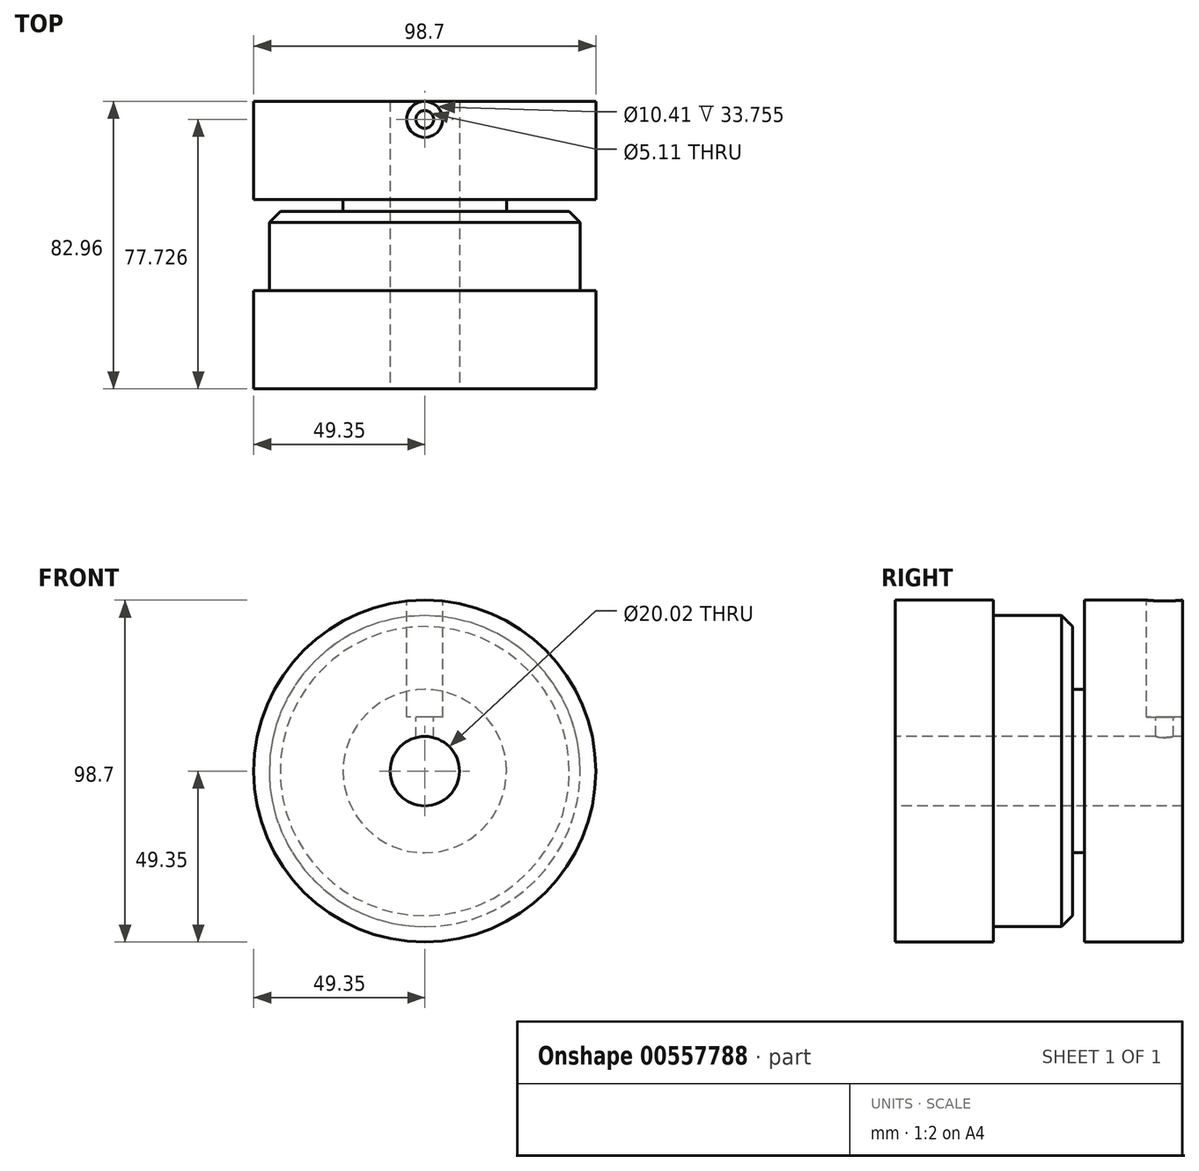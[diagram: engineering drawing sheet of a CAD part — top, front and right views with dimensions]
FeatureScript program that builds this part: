
annotation { "Feature Type Name" : "Feature", "Feature Type Description" : "" }
export const myFeature = defineFeature(function(context is Context, id is Id, definition is map)
    precondition{}
    {
        {
            var Q0;
            Q0=qCreatedBy(makeId("Right.planeOp"),FACE);
            var sketch = newSketch(context, id + "F0", { "sketchPlane" : qUnion([Q0])});
            skLineSegment(sketch, "E0", {"start": v(-35.21, 0) * mm, "end": v(33.24, 0) * mm, "construction": true});
            skLineSegment(sketch, "E1", {"start": v(0, 10) * mm, "end": v(-41.48, 10) * mm});
            skLineSegment(sketch, "E2", {"start": v(-41.48, 10) * mm, "end": v(-41.48, 49.35) * mm});
            skLineSegment(sketch, "E3", {"start": v(-41.48, 49.35) * mm, "end": v(-13.14, 49.35) * mm});
            skLineSegment(sketch, "E4", {"start": v(-13.14, 49.35) * mm, "end": v(-13.14, 44.88) * mm});
            skLineSegment(sketch, "E5", {"start": v(-13.14, 44.88) * mm, "end": v(9.72, 44.88) * mm});
            skLineSegment(sketch, "E6", {"start": v(0, 44.88) * mm, "end": v(0, 10) * mm, "construction": true});
            skLineSegment(sketch, "E7.MirrorCS", {"start": v(13.14, 49.35) * mm, "end": v(13.14, 23.57) * mm});
            skLineSegment(sketch, "E8.MirrorCS", {"start": v(41.48, 49.35) * mm, "end": v(13.14, 49.35) * mm});
            skLineSegment(sketch, "E9.MirrorCS", {"start": v(41.48, 10) * mm, "end": v(41.48, 49.35) * mm});
            skLineSegment(sketch, "E10.MirrorCS", {"start": v(0, 10) * mm, "end": v(41.48, 10) * mm});
            skLineSegment(sketch, "E11", {"start": v(9.72, 44.88) * mm, "end": v(9.72, 23.57) * mm});
            skLineSegment(sketch, "E12", {"start": v(9.72, 23.57) * mm, "end": v(14.35, 23.57) * mm});
            skPoint(sketch, "E13.orphan", {"position": v(0, 44.88) * mm});
            skSolve(sketch);
        }
        {
            var Q0;
            Q0=qSketchRegion(id+"F0",true);
            var Q1;
            Q1=sQuery(id+"F0.wireOp",EDGE,"E0");
            revolve(context, id + "F1", {"entities" : qUnion([Q0]), "axis" : qUnion([Q1]), "revolveType" : RevolveType.FULL});
        }
        {
            var Q0;
            Q0=makeQuery(id+"F1.opRevolve","SWEPT_EDGE",EDGE,{"disambiguationData":[OSD([sQuery(id+"F0.wireOp",EDGE,"cf1fef12-5ac8-4b01-91cc-4780af7254460.MirrorCS"),sQuery(id+"F0.wireOp",EDGE,"5POYRYxj-56Jz-sZJ7-dkSz-zXBiMIf3wF9C")])]});
            var Q1;
            Q1=makeQuery(id+"F1.opRevolve","SWEPT_EDGE",EDGE,{"disambiguationData":[OSD([sQuery(id+"F0.wireOp",EDGE,"E5"),sQuery(id+"F0.wireOp",EDGE,"E11")])]});
            chamfer(context, id + "F2", {"entities" : qUnion([Q0, Q1]), "width" : 3.17 * mm, "tangentPropagation" : true});
        }
        {
            var Q0;
            Q0=makeQuery(id+"F1.opRevolve","SWEPT_EDGE",EDGE,{"disambiguationData":[OSD([sQuery(id+"F0.wireOp",EDGE,"E11"),sQuery(id+"F0.wireOp",EDGE,"E12")])]});
            var Q1;
            Q1=makeQuery(id+"F1.opRevolve","SWEPT_EDGE",EDGE,{"disambiguationData":[OSD([sQuery(id+"F0.wireOp",EDGE,"E12"),sQuery(id+"F0.wireOp",EDGE,"5POYRYxj-56Jz-sZJ7-dkSz-zXBiMIf3wF9C")])]});
            fillet(context, id + "F3", {"entities" : qUnion([Q0, Q1]), "radius" : 0.25 * mm, "tangentPropagation" : true, "allowEdgeOverflow" : false});
        }
        {
            var Q0;
            Q0=qCreatedBy(makeId("Top.planeOp"),FACE);
            cPlane(context, id + "F4", {"entities" : qUnion([Q0]), "cplaneType" : CPlaneType.OFFSET, "offset" : 49.35 * mm, "width" : 152.4 * mm, "height" : 152.4 * mm});
        }
        {
            var Q0;
            Q0=qCreatedBy(id+"F4.planeOp",FACE);
            var sketch = newSketch(context, id + "F5", { "sketchPlane" : qUnion([Q0])});
            skPoint(sketch, "E14", {"position": v(0, 36.25) * mm});
            skLineSegment(sketch, "E15.0", {"start": v(49.35, 41.48) * mm, "end": v(-49.35, 41.48) * mm});
            skCircle(sketch, "E16", {"center": v(0, 36.25) * mm, "radius": 5.23 * mm, "construction": true});
            skSolve(sketch);
        }
        {
            var Q0;
            Q0=sQuery(id+"F5.wireOp",VERTEX,"E14");
            var Q1;
            Q1=makeQuery(id+"F1.opRevolve","SWEPT_BODY",BODY,{"disambiguationData":[OSD([sQuery(id+"F0.wireOp",EDGE,"E1"),sQuery(id+"F0.wireOp",EDGE,"E2"),sQuery(id+"F0.wireOp",EDGE,"E3"),sQuery(id+"F0.wireOp",EDGE,"E4"),sQuery(id+"F0.wireOp",EDGE,"E5"),sQuery(id+"F0.wireOp",EDGE,"cf1fef12-5ac8-4b01-91cc-4780af7254460.MirrorCS"),sQuery(id+"F0.wireOp",EDGE,"E7.MirrorCS"),sQuery(id+"F0.wireOp",EDGE,"E8.MirrorCS"),sQuery(id+"F0.wireOp",EDGE,"E9.MirrorCS"),sQuery(id+"F0.wireOp",EDGE,"E10.MirrorCS"),sQuery(id+"F0.wireOp",EDGE,"E11"),sQuery(id+"F0.wireOp",EDGE,"E12"),sQuery(id+"F0.wireOp",EDGE,"5POYRYxj-56Jz-sZJ7-dkSz-zXBiMIf3wF9C")])]});
            hole(context, id + "F6", {"style" : HoleStyle.C_BORE, "endStyle" : HoleEndStyle.BLIND, "holeDiameter" : 5.1 * mm, "cBoreDiameter" : 10.4 * mm, "cBoreDepth" : 33.48 * mm, "holeDepth" : 49.35 * mm, "isTappedThrough" : true, "tappedDepth" : 12.7 * mm, "tapClearance" : 3, "locations" : qUnion([Q0]), "scope" : qUnion([Q1])});
        }
    });
